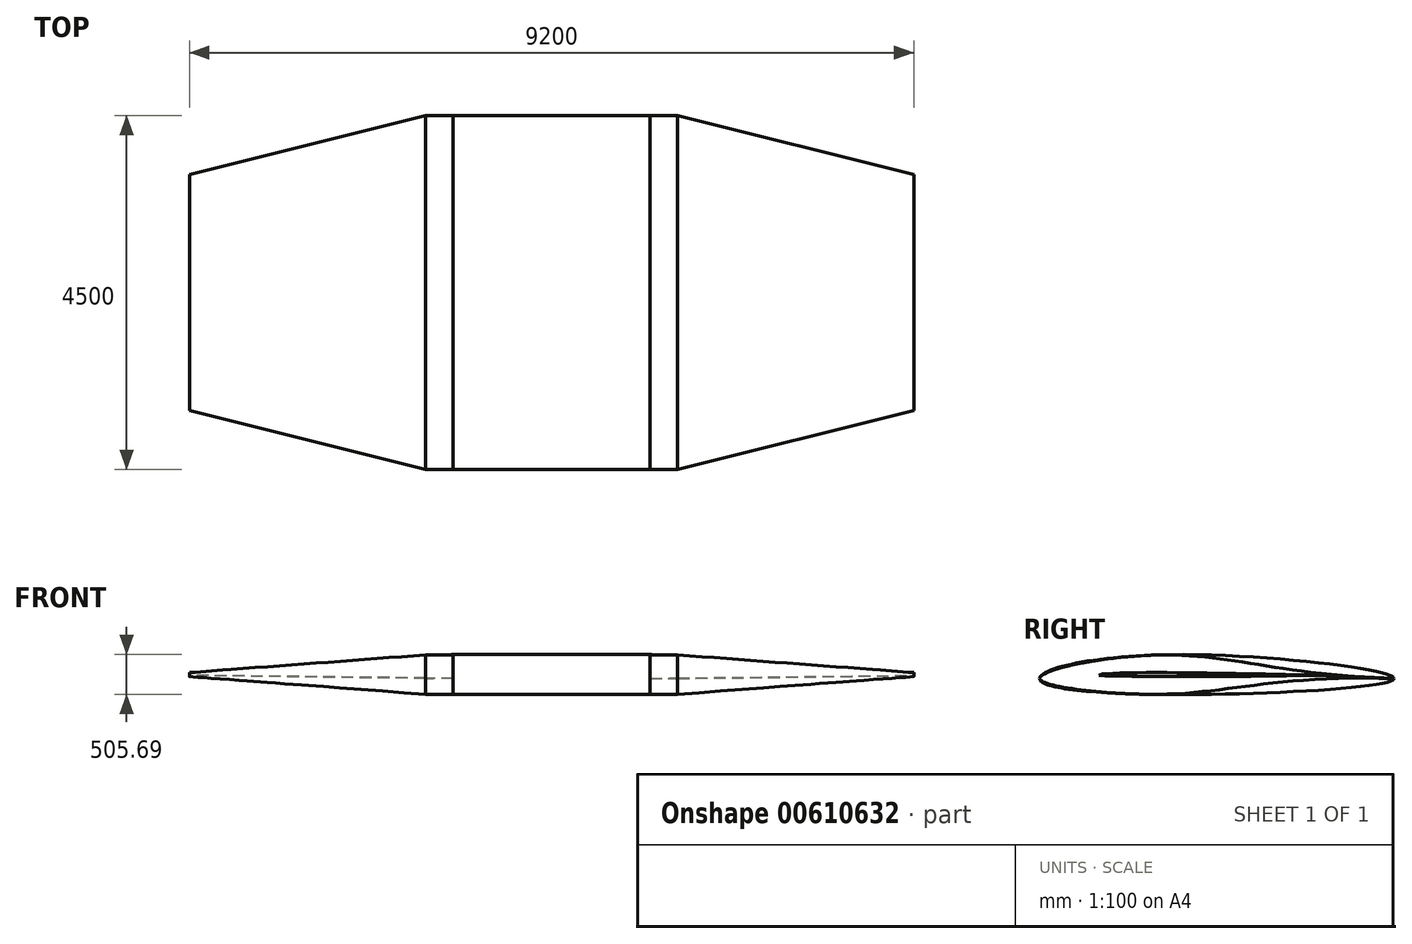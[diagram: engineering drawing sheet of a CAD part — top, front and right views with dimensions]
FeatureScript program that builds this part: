
annotation { "Feature Type Name" : "Feature", "Feature Type Description" : "" }
export const myFeature = defineFeature(function(context is Context, id is Id, definition is map)
    precondition{}
    {
        {
            var Q0;
            Q0=qCreatedBy(makeId("Right.planeOp"),FACE);
            var sketch = newSketch(context, id + "F0", { "sketchPlane" : qUnion([Q0])});
            skFitSpline(sketch, "E0", {"points": [v(-1500, -50) * mm, v(0, 250) * mm, v(3000, -50) * mm], "startDerivative": vector(0, 887.04) * mm, "endDerivative": vector(0, -631.84) * mm});
            skFitSpline(sketch, "E1", {"points": [v(-1500, -50) * mm, v(0, -250) * mm, v(3000, -50) * mm], "startDerivative": vector(0, -903.58) * mm, "endDerivative": vector(0, 641.04) * mm});
            skSolve(sketch);
        }
        {
            var Q0;
            Q0=qCreatedBy(makeId("Right.planeOp"),FACE);
            cPlane(context, id + "F1", {"entities" : qUnion([Q0]), "cplaneType" : CPlaneType.OFFSET, "offset" : 1600 * mm, "oppositeDirection" : true, "width" : 150 * mm, "height" : 150 * mm});
        }
        {
            var Q0;
            Q0=qCreatedBy(id+"F1.planeOp",FACE);
            var sketch = newSketch(context, id + "F2", { "sketchPlane" : qUnion([Q0])});
            skFitSpline(sketch, "E2", {"points": [v(-1500, -50) * mm, v(0, 250) * mm, v(3000, -50) * mm], "startDerivative": vector(0, 887.04) * mm, "endDerivative": vector(7705.35, -256.85) * mm});
            skFitSpline(sketch, "E3", {"points": [v(-1500, -50) * mm, v(0, -250) * mm, v(3000, -50) * mm], "startDerivative": vector(0, -722.87) * mm, "endDerivative": vector(7692.49, -256.42) * mm});
            skSolve(sketch);
        }
        {
            var Q0;
            Q0=qCreatedBy(makeId("Right.planeOp"),FACE);
            cPlane(context, id + "F3", {"entities" : qUnion([Q0]), "cplaneType" : CPlaneType.OFFSET, "offset" : 1600 * mm, "width" : 150 * mm, "height" : 150 * mm});
        }
        {
            var Q0;
            Q0=qCreatedBy(id+"F3.planeOp",FACE);
            var sketch = newSketch(context, id + "F4", { "sketchPlane" : qUnion([Q0])});
            skFitSpline(sketch, "E4", {"points": [v(-1500, -50) * mm, v(0, 250) * mm, v(3000, -50) * mm], "startDerivative": vector(0, 887.04) * mm, "endDerivative": vector(7705.35, -256.85) * mm});
            skFitSpline(sketch, "E5", {"points": [v(-1500, -50) * mm, v(0, -250) * mm, v(3000, -50) * mm], "startDerivative": vector(0, -722.87) * mm, "endDerivative": vector(7692.49, -256.42) * mm});
            skSolve(sketch);
        }
        {
            var Q0;
            Q0=qCreatedBy(makeId("Right.planeOp"),FACE);
            cPlane(context, id + "F5", {"entities" : qUnion([Q0]), "cplaneType" : CPlaneType.OFFSET, "offset" : 4600 * mm, "oppositeDirection" : true, "width" : 150 * mm, "height" : 150 * mm});
        }
        {
            var Q0;
            Q0=qCreatedBy(id+"F5.planeOp",FACE);
            var sketch = newSketch(context, id + "F6", { "sketchPlane" : qUnion([Q0])});
            skFitSpline(sketch, "E6", {"points": [v(-750, -10) * mm, v(250, 25) * mm, v(2250, -10) * mm], "startDerivative": vector(0, 253.46) * mm, "endDerivative": vector(3841.36, -51.22) * mm});
            skFitSpline(sketch, "E7", {"points": [v(-750, -10) * mm, v(750, -25) * mm, v(2250, -10) * mm], "startDerivative": vector(0, -45) * mm, "endDerivative": vector(4500, 0) * mm});
            skSolve(sketch);
        }
        {
            var Q0;
            Q0=qCreatedBy(makeId("Right.planeOp"),FACE);
            cPlane(context, id + "F7", {"entities" : qUnion([Q0]), "cplaneType" : CPlaneType.OFFSET, "offset" : 4600 * mm, "width" : 150 * mm, "height" : 150 * mm});
        }
        {
            var Q0;
            Q0=qCreatedBy(id+"F7.planeOp",FACE);
            var sketch = newSketch(context, id + "F8", { "sketchPlane" : qUnion([Q0])});
            skFitSpline(sketch, "E8", {"points": [v(-750, -10) * mm, v(250, 25) * mm, v(2250, -10) * mm], "startDerivative": vector(0, 253.46) * mm, "endDerivative": vector(3841.36, -51.22) * mm});
            skFitSpline(sketch, "E9", {"points": [v(-750, -10) * mm, v(750, -25) * mm, v(2250, -10) * mm], "startDerivative": vector(0, -45) * mm, "endDerivative": vector(4500, 0) * mm});
            skSolve(sketch);
        }
        {
            var Q0;
            Q0=makeQuery(id+"F0.imprint","IMPRINT",FACE,{"disambiguationData":[TD([[makeQuery(id+"F0.imprint","IMPRINT",EDGE,{"derivedFrom":sQuery(id+"F0.wireOp",EDGE,"E0")}),-1.0]])]});
            extrude(context, id + "F9", {"entities" : qUnion([Q0]), "endBound" : BoundingType.SYMMETRIC, "depth" : 2500 * mm, "offsetDistance" : 25 * mm});
        }
        {
            var Q1;
            Q1=makeQuery(id+"F9.opExtrude","CAP_FACE",FACE,{"disambiguationData":[OSD([sQuery(id+"F0.wireOp",EDGE,"E0"),sQuery(id+"F0.wireOp",EDGE,"E1")])],"isStart":true});
            var Q2;
            {var subQ0=sQuery(id+"F2.wireOp",EDGE,"E2");Q2=makeQuery(id+"F2.imprint","IMPRINT",FACE,{"disambiguationData":[TD([[makeQuery(id+"F2.imprint","IMPRINT",EDGE,{"derivedFrom":subQ0}),-1.0]])]});}
            loft(context, id + "F10", {"operationType" : NewBodyOperationType.ADD, "sheetProfilesArray" : [{ "sheetProfileEntities" : qUnion([Q1]) }, { "sheetProfileEntities" : qUnion([Q2]) }]});
        }
        {
            var Q1;
            Q1=makeQuery(id+"F9.opExtrude","CAP_FACE",FACE,{"disambiguationData":[OSD([sQuery(id+"F0.wireOp",EDGE,"E0"),sQuery(id+"F0.wireOp",EDGE,"E1")])],"isStart":false});
            var Q2;
            {var subQ0=sQuery(id+"F4.wireOp",EDGE,"E4");Q2=makeQuery(id+"F4.imprint","IMPRINT",FACE,{"disambiguationData":[TD([[makeQuery(id+"F4.imprint","IMPRINT",EDGE,{"derivedFrom":subQ0}),-1.0]])]});}
            loft(context, id + "F11", {"operationType" : NewBodyOperationType.ADD, "sheetProfilesArray" : [{ "sheetProfileEntities" : qUnion([Q1]) }, { "sheetProfileEntities" : qUnion([Q2]) }]});
        }
        {
            var Q1;
            {var subQ0=sQuery(id+"F2.wireOp",EDGE,"E2");Q1=makeQuery(id+"F10.opLoft","CAP_FACE",FACE,{"disambiguationData":[OSD([makeQuery(id+"F2.imprint","IMPRINT",FACE,{"disambiguationData":[TD([[makeQuery(id+"F2.imprint","IMPRINT",EDGE,{"derivedFrom":subQ0}),-1.0]])]})])],"isStart":true});}
            var Q2;
            Q2=makeQuery(id+"F6.imprint","IMPRINT",FACE,{"disambiguationData":[TD([[makeQuery(id+"F6.imprint","IMPRINT",EDGE,{"derivedFrom":sQuery(id+"F6.wireOp",EDGE,"E6")}),-1.0]])]});
            loft(context, id + "F12", {"operationType" : NewBodyOperationType.ADD, "sheetProfilesArray" : [{ "sheetProfileEntities" : qUnion([Q1]) }, { "sheetProfileEntities" : qUnion([Q2]) }]});
        }
        {
            var Q1;
            {var subQ0=sQuery(id+"F4.wireOp",EDGE,"E4");Q1=makeQuery(id+"F11.opLoft","CAP_FACE",FACE,{"disambiguationData":[OSD([makeQuery(id+"F4.imprint","IMPRINT",FACE,{"disambiguationData":[TD([[makeQuery(id+"F4.imprint","IMPRINT",EDGE,{"derivedFrom":subQ0}),-1.0]])]})])],"isStart":true});}
            var Q2;
            Q2=makeQuery(id+"F8.imprint","IMPRINT",FACE,{"disambiguationData":[TD([[makeQuery(id+"F8.imprint","IMPRINT",EDGE,{"derivedFrom":sQuery(id+"F8.wireOp",EDGE,"E8")}),-1.0]])]});
            loft(context, id + "F13", {"operationType" : NewBodyOperationType.ADD, "sheetProfilesArray" : [{ "sheetProfileEntities" : qUnion([Q1]) }, { "sheetProfileEntities" : qUnion([Q2]) }]});
        }
    });
